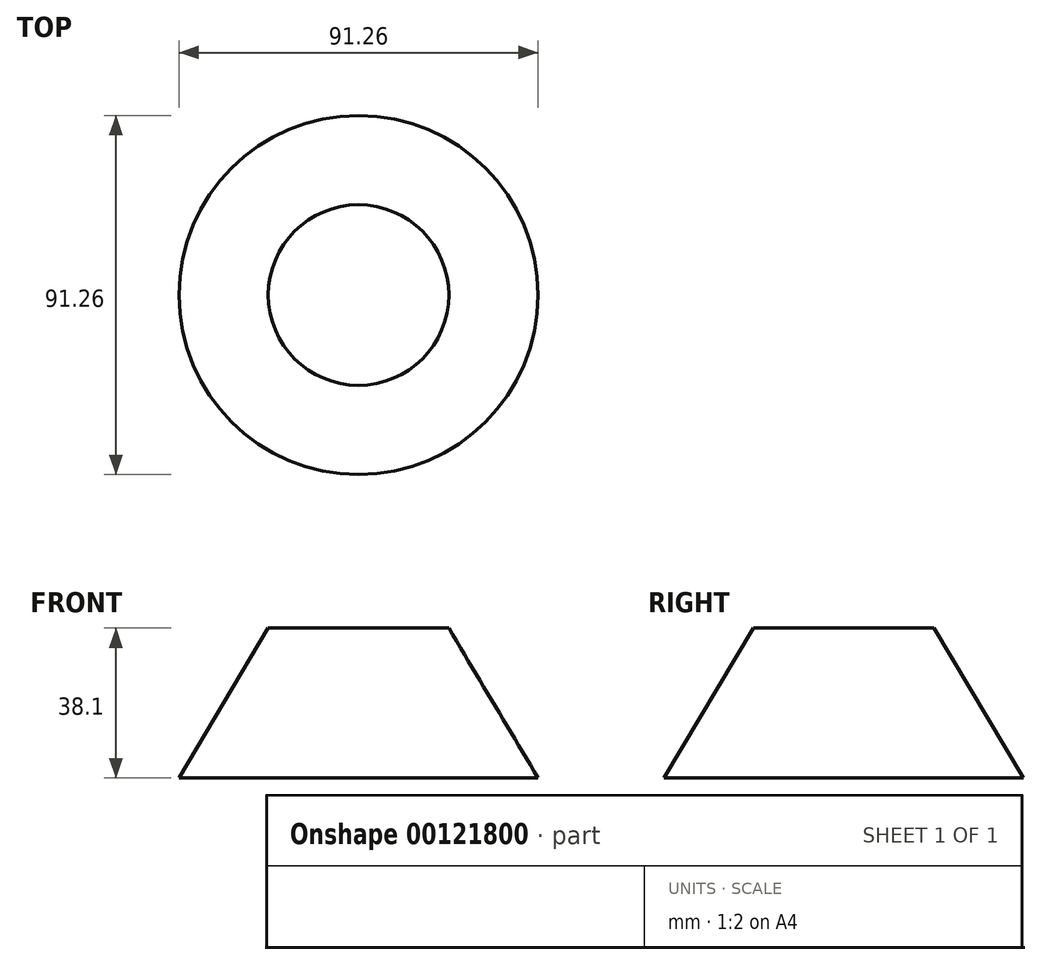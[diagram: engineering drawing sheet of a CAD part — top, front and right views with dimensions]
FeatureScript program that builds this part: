
annotation { "Feature Type Name" : "Feature", "Feature Type Description" : "" }
export const myFeature = defineFeature(function(context is Context, id is Id, definition is map)
    precondition{}
    {
        {
            var Q0;
            Q0=qCreatedBy(makeId("Top.planeOp"),FACE);
            var sketch = newSketch(context, id + "F0", { "sketchPlane" : qUnion([Q0])});
            skCircle(sketch, "E0", {"center": v(0, 0) * mm, "radius": 45.63 * mm});
            skSolve(sketch);
        }
        {
            var Q0;
            Q0=makeQuery(id+"F0.imprint","IMPRINT",FACE,{"disambiguationData":[TD([[makeQuery(id+"F0.imprint","IMPRINT",EDGE,{"derivedFrom":sQuery(id+"F0.wireOp",EDGE,"E0")}),1.0]])]});
            cPlane(context, id + "F1", {"entities" : qUnion([Q0]), "cplaneType" : CPlaneType.OFFSET, "offset" : 38.1 * mm, "width" : 152.4 * mm, "height" : 152.4 * mm});
        }
        {
            var Q0;
            Q0=qCreatedBy(id+"F1.planeOp",FACE);
            var sketch = newSketch(context, id + "F2", { "sketchPlane" : qUnion([Q0])});
            skCircle(sketch, "E1", {"center": v(0, 0) * mm, "radius": 22.93 * mm});
            skSolve(sketch);
        }
        {
            var Q0;
            Q0=makeQuery(id+"F0.imprint","IMPRINT",FACE,{"disambiguationData":[TD([[makeQuery(id+"F0.imprint","IMPRINT",EDGE,{"derivedFrom":sQuery(id+"F0.wireOp",EDGE,"E0")}),1.0]])]});
            var Q1;
            Q1=makeQuery(id+"F2.imprint","IMPRINT",FACE,{"disambiguationData":[TD([[makeQuery(id+"F2.imprint","IMPRINT",EDGE,{"derivedFrom":sQuery(id+"F2.wireOp",EDGE,"E1")}),1.0]])]});
            loft(context, id + "F3", {"sheetProfilesArray" : [{ "sheetProfileEntities" : qUnion([Q0]) }, { "sheetProfileEntities" : qUnion([Q1]) }]});
        }
    });
